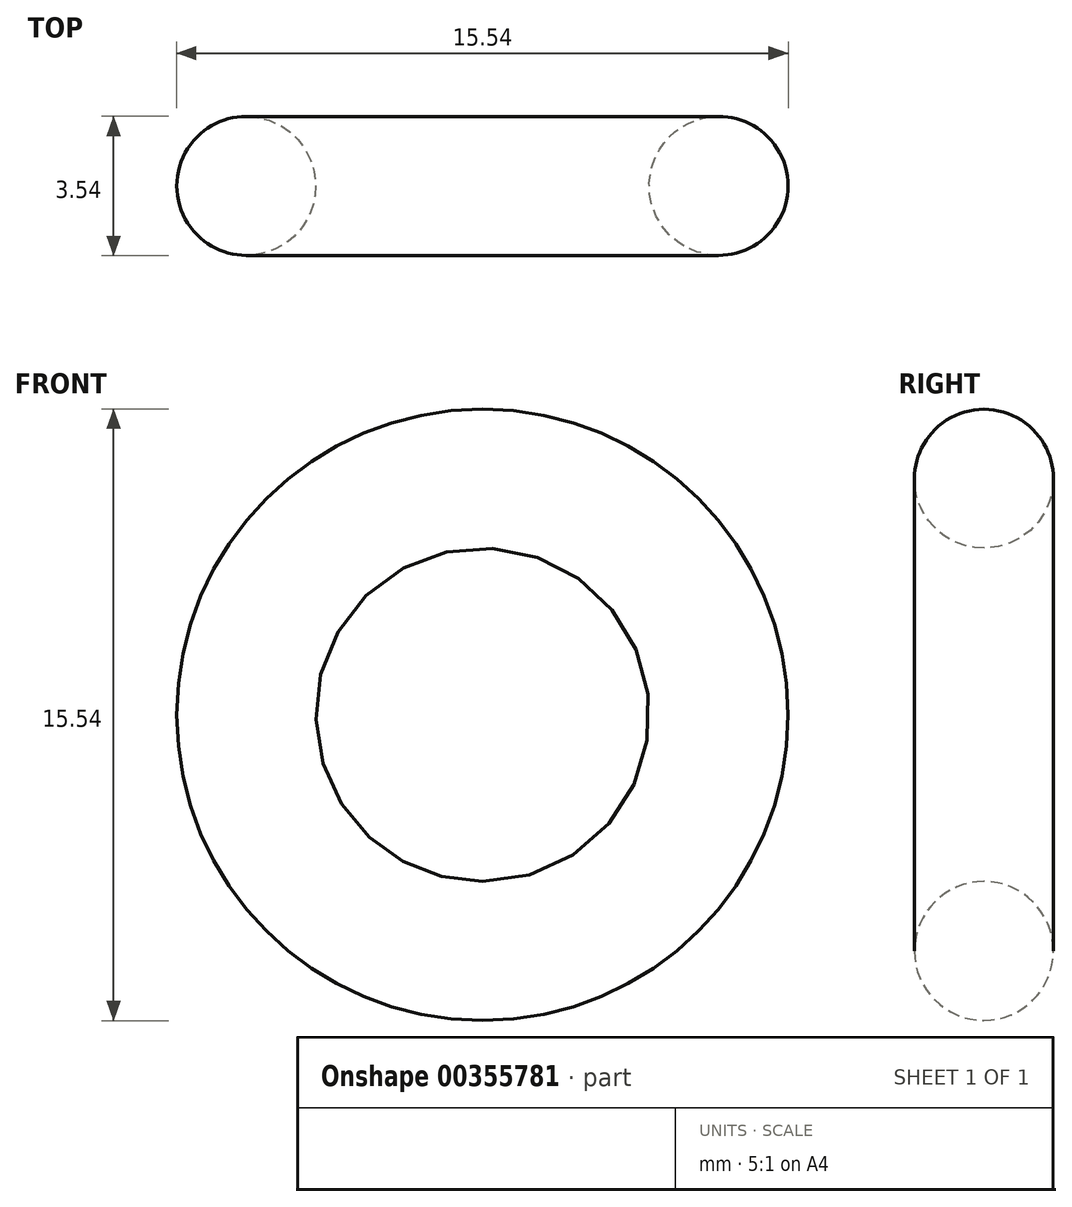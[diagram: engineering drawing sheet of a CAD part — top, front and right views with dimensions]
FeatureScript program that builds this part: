
annotation { "Feature Type Name" : "Feature", "Feature Type Description" : "" }
export const myFeature = defineFeature(function(context is Context, id is Id, definition is map)
    precondition{}
    {
        {
            var Q0;
            Q0=qCreatedBy(makeId("Front.planeOp"),FACE);
            var sketch = newSketch(context, id + "F0", { "sketchPlane" : qUnion([Q0])});
            skCircle(sketch, "E0", {"center": v(0, 0) * mm, "radius": 6 * mm});
            skSolve(sketch);
        }
        {
            var Q0;
            Q0=qCreatedBy(makeId("Right.planeOp"),FACE);
            var sketch = newSketch(context, id + "F1", { "sketchPlane" : qUnion([Q0])});
            skLineSegment(sketch, "E1.0", {"start": v(0, -6) * mm, "end": v(0, 6) * mm});
            skCircle(sketch, "E2", {"center": v(0, 6) * mm, "radius": 1.76 * mm});
            skSolve(sketch);
        }
        {
            var Q0;
            Q0=makeQuery(id+"F1.imprint","IMPRINT",FACE,{"disambiguationData":[TD([[makeQuery(id+"F1.imprint","IMPRINT",EDGE,{"derivedFrom":sQuery(id+"F1.wireOp",EDGE,"E2")}),1.0]])]});
            var Q1;
            Q1=sQuery(id+"F0.wireOp",EDGE,"E0");
            sweep(context, id + "F2", {"profiles" : qUnion([Q0]), "path" : qUnion([Q1])});
        }
    });
